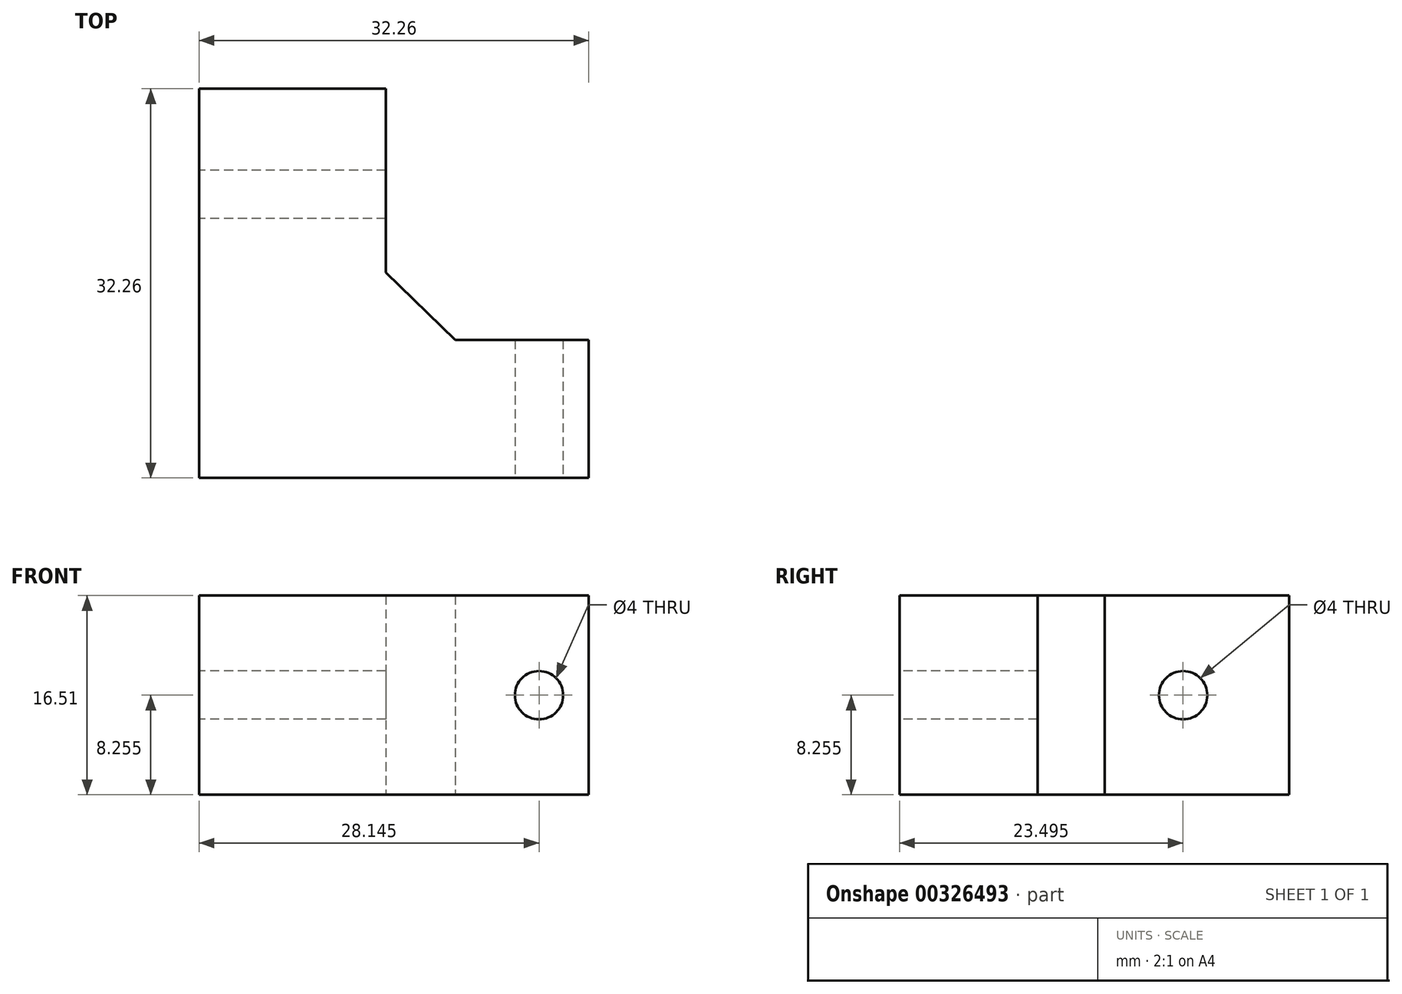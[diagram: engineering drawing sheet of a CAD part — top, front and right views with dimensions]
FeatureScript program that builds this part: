
annotation { "Feature Type Name" : "Feature", "Feature Type Description" : "" }
export const myFeature = defineFeature(function(context is Context, id is Id, definition is map)
    precondition{}
    {
        {
            var Q0;
            Q0=qCreatedBy(makeId("Top.planeOp"),FACE);
            var sketch = newSketch(context, id + "F0", { "sketchPlane" : qUnion([Q0])});
            skLineSegment(sketch, "E0", {"start": v(0, 0) * mm, "end": v(-32.26, 0) * mm});
            skLineSegment(sketch, "E1", {"start": v(-32.26, 0) * mm, "end": v(-32.26, 32.26) * mm});
            skPoint(sketch, "E2", {"position": v(-7.62, 0) * mm});
            skLineSegment(sketch, "E3", {"start": v(0, 11.43) * mm, "end": v(0, 0) * mm});
            skLineSegment(sketch, "E4", {"start": v(0, 11.43) * mm, "end": v(-11.06, 11.43) * mm});
            skPoint(sketch, "E5", {"position": v(-32.26, 24.64) * mm});
            skLineSegment(sketch, "E6", {"start": v(-32.26, 32.26) * mm, "end": v(-20.83, 32.26) * mm});
            skLineSegment(sketch, "E7", {"start": v(-20.83, 32.26) * mm, "end": v(-20.7, 20.83) * mm});
            skLineSegment(sketch, "E8.bottom", {"start": v(-20.83, 32.26) * mm, "end": v(-43.69, 32.26) * mm});
            skLineSegment(sketch, "E8.top", {"start": v(-20.83, 17.02) * mm, "end": v(-43.69, 17.02) * mm});
            skLineSegment(sketch, "E8.left", {"start": v(-20.83, 32.26) * mm, "end": v(-20.83, 17.02) * mm});
            skLineSegment(sketch, "E8.right", {"start": v(-43.69, 32.26) * mm, "end": v(-43.69, 17.02) * mm});
            skLineSegment(sketch, "E9", {"start": v(-20.83, 17.02) * mm, "end": v(-16.8, 17.02) * mm});
            skLineSegment(sketch, "E10", {"start": v(-16.8, 17.02) * mm, "end": v(-11.06, 11.43) * mm});
            skLineSegment(sketch, "E11.bottom", {"start": v(-16.8, 17.02) * mm, "end": v(-32.26, 17.02) * mm});
            skLineSegment(sketch, "E11.top", {"start": v(-16.8, 32.26) * mm, "end": v(-32.26, 32.26) * mm});
            skLineSegment(sketch, "E11.left", {"start": v(-16.8, 17.02) * mm, "end": v(-16.8, 32.26) * mm});
            skLineSegment(sketch, "E11.right", {"start": v(-32.26, 17.02) * mm, "end": v(-32.26, 32.26) * mm});
            skSolve(sketch);
        }
        {
            var Q0;
            Q0=makeQuery(id+"F0.imprint","IMPRINT",FACE,{"disambiguationData":[TD([[makeQuery(id+"F0.imprint","IMPRINT",EDGE,{"derivedFrom":sQuery(id+"F0.wireOp",EDGE,"E0")}),-1.0]])]});
            var Q1;
            {var subQ0=sQuery(id+"F0.wireOp",EDGE,"E8.left");Q1=makeQuery(id+"F0.imprint","IMPRINT",FACE,{"disambiguationData":[TD([[makeQuery(id+"F0.imprint","IMPRINT",EDGE,{"derivedFrom":subQ0}),-1.0]])]});}
            var Q2;
            {var subQ0=sQuery(id+"F0.wireOp",EDGE,"E8.left");Q2=makeQuery(id+"F0.imprint","IMPRINT",FACE,{"disambiguationData":[TD([[makeQuery(id+"F0.imprint","IMPRINT",EDGE,{"derivedFrom":subQ0}),1.0]])]});}
            extrude(context, id + "F1", {"entities" : qUnion([Q0, Q1, Q2]), "depth" : 16.5 * mm});
        }
        {
            var Q0;
            Q0=makeQuery(id+"F1.opExtrude","SWEPT_FACE",FACE,{"disambiguationData":[OSD([sQuery(id+"F0.wireOp",EDGE,"E0")])]});
            var sketch = newSketch(context, id + "F2", { "sketchPlane" : qUnion([Q0])});
            skLineSegment(sketch, "E12", {"start": v(-4.11, 8.26) * mm, "end": v(-32.26, 8.26) * mm});
            skPoint(sketch, "E12.startSnap0", {"position": v(-32.26, 8.26) * mm});
            skSolve(sketch);
        }
        {
            var Q0;
            Q0=sQuery(id+"F2.wireOp",VERTEX,"E12.start");
            var Q1;
            Q1=makeQuery(id+"F1.opExtrude","SWEPT_BODY",BODY,{"disambiguationData":[OSD([sQuery(id+"F0.wireOp",EDGE,"E0"),sQuery(id+"F0.wireOp",EDGE,"E1"),sQuery(id+"F0.wireOp",EDGE,"E3"),sQuery(id+"F0.wireOp",EDGE,"E4"),sQuery(id+"F0.wireOp",EDGE,"E6"),sQuery(id+"F0.wireOp",EDGE,"E7"),sQuery(id+"F0.wireOp",EDGE,"2L7WUZFq-deW9-Yjwo-kVYH-NKvs7UjgcPIr")])]});
            hole(context, id + "F3", {"style" : HoleStyle.SIMPLE, "endStyle" : HoleEndStyle.THROUGH, "holeDiameter" : 4 * mm, "tappedDepth" : 12.7 * mm, "tapClearance" : 3, "locations" : qUnion([Q0]), "scope" : qUnion([Q1])});
        }
        {
            var Q0;
            Q0=makeQuery(id+"F1.opExtrude","SWEPT_FACE",FACE,{"disambiguationData":[OSD([sQuery(id+"F0.wireOp",EDGE,"E1")])]});
            var sketch = newSketch(context, id + "F4", { "sketchPlane" : qUnion([Q0])});
            skLineSegment(sketch, "E13", {"start": v(0, 8.26) * mm, "end": v(-23.5, 8.26) * mm});
            skPoint(sketch, "E14", {"position": v(-23.5, 8.26) * mm});
            skSolve(sketch);
        }
        {
            var Q0;
            Q0=sQuery(id+"F4.wireOp",VERTEX,"E14");
            var Q1;
            Q1=makeQuery(id+"F1.opExtrude","SWEPT_BODY",BODY,{"disambiguationData":[OSD([sQuery(id+"F0.wireOp",EDGE,"E0"),sQuery(id+"F0.wireOp",EDGE,"E1"),sQuery(id+"F0.wireOp",EDGE,"E3"),sQuery(id+"F0.wireOp",EDGE,"E4"),sQuery(id+"F0.wireOp",EDGE,"E6"),sQuery(id+"F0.wireOp",EDGE,"E7"),sQuery(id+"F0.wireOp",EDGE,"2L7WUZFq-deW9-Yjwo-kVYH-NKvs7UjgcPIr")])]});
            hole(context, id + "F5", {"style" : HoleStyle.SIMPLE, "endStyle" : HoleEndStyle.THROUGH, "holeDiameter" : 4 * mm, "tappedDepth" : 12.7 * mm, "tapClearance" : 3, "locations" : qUnion([Q0]), "scope" : qUnion([Q1])});
        }
    });
